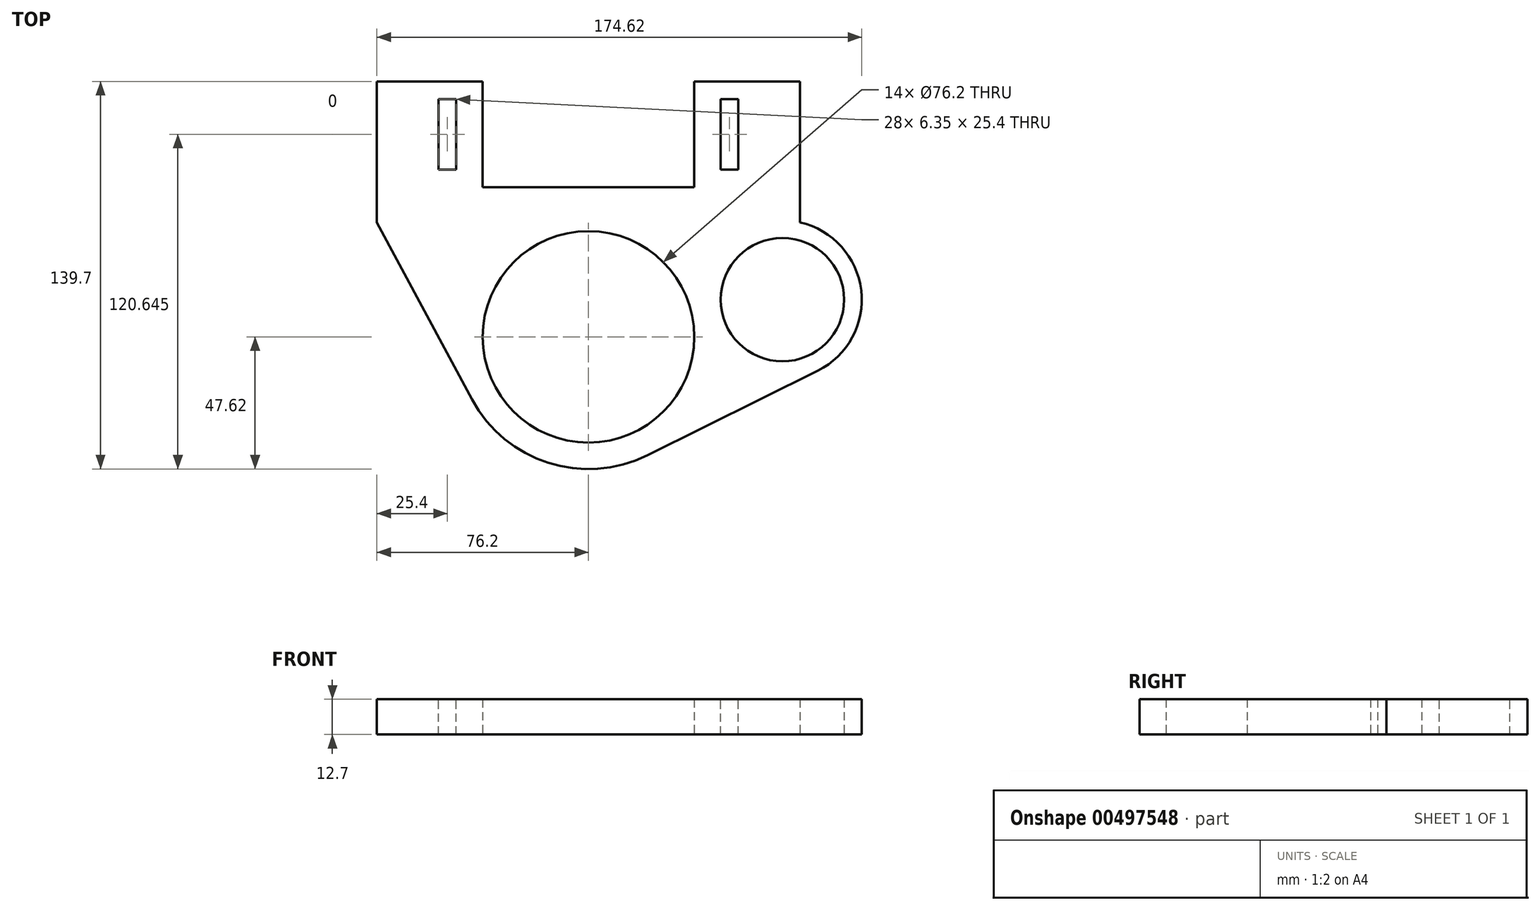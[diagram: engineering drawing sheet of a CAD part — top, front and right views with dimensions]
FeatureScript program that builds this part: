
annotation { "Feature Type Name" : "Feature", "Feature Type Description" : "" }
export const myFeature = defineFeature(function(context is Context, id is Id, definition is map)
    precondition{}
    {
        {
            var Q0;
            Q0=qCreatedBy(makeId("Top.planeOp"),FACE);
            var sketch = newSketch(context, id + "F0", { "sketchPlane" : qUnion([Q0])});
            skArc(sketch, "E0", {"start": v(-41.96, -22.52) * mm, "mid": v(-14.47, -45.37) * mm, "end": v(21.18, -42.66) * mm});
            skLineSegment(sketch, "E1", {"start": v(-76.2, 41.27) * mm, "end": v(-76.2, 92.07) * mm});
            skLineSegment(sketch, "E2", {"start": v(-76.2, 41.27) * mm, "end": v(-41.96, -22.52) * mm});
            skLineSegment(sketch, "E3", {"start": v(76.2, 41.27) * mm, "end": v(76.2, 92.08) * mm});
            skLineSegment(sketch, "E4", {"start": v(76.2, 92.08) * mm, "end": v(38.1, 92.08) * mm});
            skLineSegment(sketch, "E5", {"start": v(38.1, 92.08) * mm, "end": v(38.1, 53.98) * mm});
            skLineSegment(sketch, "E6", {"start": v(38.1, 53.98) * mm, "end": v(-38.1, 53.97) * mm});
            skLineSegment(sketch, "E7", {"start": v(-38.1, 53.97) * mm, "end": v(-38.1, 92.08) * mm});
            skLineSegment(sketch, "E8", {"start": v(-38.1, 92.07) * mm, "end": v(-76.2, 92.07) * mm});
            skCircle(sketch, "E9", {"center": v(0, 0) * mm, "radius": 38.1 * mm});
            skCircle(sketch, "E10", {"center": v(69.85, 13.41) * mm, "radius": 22.23 * mm});
            skArc(sketch, "E11", {"start": v(82.56, -12.18) * mm, "mid": v(98.22, 16.79) * mm, "end": v(76.2, 41.28) * mm});
            skLineSegment(sketch, "E12", {"start": v(21.18, -42.66) * mm, "end": v(82.56, -12.18) * mm});
            skSolve(sketch);
        }
        {
            var Q0;
            Q0=makeQuery(id+"F0.imprint","IMPRINT",FACE,{"disambiguationData":[TD([[makeQuery(id+"F0.imprint","IMPRINT",EDGE,{"derivedFrom":sQuery(id+"F0.wireOp",EDGE,"E0")}),1.0]])]});
            extrude(context, id + "F1", {"entities" : qUnion([Q0]), "depth" : 12.7 * mm});
        }
        {
            var Q0;
            Q0=makeQuery(id+"F1.opExtrude","CAP_FACE",FACE,{"disambiguationData":[OSD([sQuery(id+"F0.wireOp",EDGE,"E0"),sQuery(id+"F0.wireOp",EDGE,"JDvhOo6X-4RoY-ADFJ-93jr-YEXSujJD0AFD"),sQuery(id+"F0.wireOp",EDGE,"LhqN19Xm-68H7-qz4W-sRNP-0HxhLSEJU9x7"),sQuery(id+"F0.wireOp",EDGE,"E1"),sQuery(id+"F0.wireOp",EDGE,"E2"),sQuery(id+"F0.wireOp",EDGE,"Ns03PbSo-hTaF-wzUj-g2w3-u53FivleiJMs"),sQuery(id+"F0.wireOp",EDGE,"E3"),sQuery(id+"F0.wireOp",EDGE,"E4"),sQuery(id+"F0.wireOp",EDGE,"E5"),sQuery(id+"F0.wireOp",EDGE,"E6"),sQuery(id+"F0.wireOp",EDGE,"E7"),sQuery(id+"F0.wireOp",EDGE,"E8"),sQuery(id+"F0.wireOp",EDGE,"E9"),sQuery(id+"F0.wireOp",EDGE,"E10")])],"isStart":false});
            var sketch = newSketch(context, id + "F2", { "sketchPlane" : qUnion([Q0])});
            skCircle(sketch, "E13", {"center": v(0, 0) * mm, "radius": 41.28 * mm});
            skCircle(sketch, "E14", {"center": v(0, 0) * mm, "radius": 38.1 * mm});
            skSolve(sketch);
        }
        {
            var Q0;
            Q0=makeQuery(id+"F1.opExtrude","CAP_FACE",FACE,{"disambiguationData":[OSD([sQuery(id+"F0.wireOp",EDGE,"E0"),sQuery(id+"F0.wireOp",EDGE,"JDvhOo6X-4RoY-ADFJ-93jr-YEXSujJD0AFD"),sQuery(id+"F0.wireOp",EDGE,"LhqN19Xm-68H7-qz4W-sRNP-0HxhLSEJU9x7"),sQuery(id+"F0.wireOp",EDGE,"E1"),sQuery(id+"F0.wireOp",EDGE,"E2"),sQuery(id+"F0.wireOp",EDGE,"Ns03PbSo-hTaF-wzUj-g2w3-u53FivleiJMs"),sQuery(id+"F0.wireOp",EDGE,"E3"),sQuery(id+"F0.wireOp",EDGE,"E4"),sQuery(id+"F0.wireOp",EDGE,"E5"),sQuery(id+"F0.wireOp",EDGE,"E6"),sQuery(id+"F0.wireOp",EDGE,"E7"),sQuery(id+"F0.wireOp",EDGE,"E8"),sQuery(id+"F0.wireOp",EDGE,"E9"),sQuery(id+"F0.wireOp",EDGE,"E10")])],"isStart":false});
            var sketch = newSketch(context, id + "F3", { "sketchPlane" : qUnion([Q0])});
            skCircle(sketch, "E15", {"center": v(69.85, 13.41) * mm, "radius": 25.4 * mm});
            skCircle(sketch, "E16", {"center": v(69.85, 13.41) * mm, "radius": 22.23 * mm});
            skSolve(sketch);
        }
        {
            var Q0;
            Q0=makeQuery(id+"F1.opExtrude","CAP_FACE",FACE,{"disambiguationData":[OSD([sQuery(id+"F0.wireOp",EDGE,"E0"),sQuery(id+"F0.wireOp",EDGE,"E1"),sQuery(id+"F0.wireOp",EDGE,"E2"),sQuery(id+"F0.wireOp",EDGE,"E3"),sQuery(id+"F0.wireOp",EDGE,"E4"),sQuery(id+"F0.wireOp",EDGE,"E5"),sQuery(id+"F0.wireOp",EDGE,"E6"),sQuery(id+"F0.wireOp",EDGE,"E7"),sQuery(id+"F0.wireOp",EDGE,"E8"),sQuery(id+"F0.wireOp",EDGE,"E9"),sQuery(id+"F0.wireOp",EDGE,"E10"),sQuery(id+"F0.wireOp",EDGE,"E11"),sQuery(id+"F0.wireOp",EDGE,"E12")])],"isStart":false});
            var sketch = newSketch(context, id + "F4", { "sketchPlane" : qUnion([Q0])});
            skLineSegment(sketch, "E17.bottom", {"start": v(-53.98, 85.72) * mm, "end": v(-47.63, 85.72) * mm});
            skLineSegment(sketch, "E17.top", {"start": v(-53.98, 60.32) * mm, "end": v(-47.62, 60.32) * mm});
            skLineSegment(sketch, "E17.left", {"start": v(-53.98, 85.72) * mm, "end": v(-53.98, 60.32) * mm});
            skLineSegment(sketch, "E17.right", {"start": v(-47.63, 85.72) * mm, "end": v(-47.63, 60.32) * mm});
            skPoint(sketch, "E18", {"position": v(-50.8, 85.72) * mm});
            skSolve(sketch);
        }
        {
            var Q0;
            Q0=makeQuery(id+"F4.imprint","IMPRINT",FACE,{"disambiguationData":[TD([[makeQuery(id+"F4.imprint","IMPRINT",EDGE,{"derivedFrom":sQuery(id+"F4.wireOp",EDGE,"E17.bottom")}),-1.0]])]});
            extrude(context, id + "F5", {"entities" : qUnion([Q0]), "operationType" : NewBodyOperationType.REMOVE, "endBound" : BoundingType.UP_TO_NEXT, "oppositeDirection" : true, "depth" : 25.4 * mm, "offsetDistance" : 25.4 * mm});
        }
        {
            var Q0;
            Q0=makeQuery(id+"F1.opExtrude","CAP_FACE",FACE,{"disambiguationData":[OSD([sQuery(id+"F0.wireOp",EDGE,"E0"),sQuery(id+"F0.wireOp",EDGE,"E1"),sQuery(id+"F0.wireOp",EDGE,"E2"),sQuery(id+"F0.wireOp",EDGE,"E3"),sQuery(id+"F0.wireOp",EDGE,"E4"),sQuery(id+"F0.wireOp",EDGE,"E5"),sQuery(id+"F0.wireOp",EDGE,"E6"),sQuery(id+"F0.wireOp",EDGE,"E7"),sQuery(id+"F0.wireOp",EDGE,"E8"),sQuery(id+"F0.wireOp",EDGE,"E9"),sQuery(id+"F0.wireOp",EDGE,"E10"),sQuery(id+"F0.wireOp",EDGE,"E11"),sQuery(id+"F0.wireOp",EDGE,"E12")])],"isStart":false});
            var sketch = newSketch(context, id + "F6", { "sketchPlane" : qUnion([Q0])});
            skLineSegment(sketch, "E19.bottom", {"start": v(47.62, 85.73) * mm, "end": v(53.98, 85.73) * mm});
            skLineSegment(sketch, "E19.top", {"start": v(47.62, 60.33) * mm, "end": v(53.98, 60.33) * mm});
            skLineSegment(sketch, "E19.left", {"start": v(47.62, 85.73) * mm, "end": v(47.62, 60.33) * mm});
            skLineSegment(sketch, "E19.right", {"start": v(53.97, 85.73) * mm, "end": v(53.97, 60.33) * mm});
            skPoint(sketch, "E20", {"position": v(50.8, 85.73) * mm});
            skSolve(sketch);
        }
        {
            var Q0;
            Q0=makeQuery(id+"F6.imprint","IMPRINT",FACE,{"disambiguationData":[TD([[makeQuery(id+"F6.imprint","IMPRINT",EDGE,{"derivedFrom":sQuery(id+"F6.wireOp",EDGE,"E19.bottom")}),-1.0]])]});
            extrude(context, id + "F7", {"entities" : qUnion([Q0]), "operationType" : NewBodyOperationType.REMOVE, "endBound" : BoundingType.UP_TO_NEXT, "oppositeDirection" : true, "depth" : 25.4 * mm, "offsetDistance" : 25.4 * mm});
        }
    });
